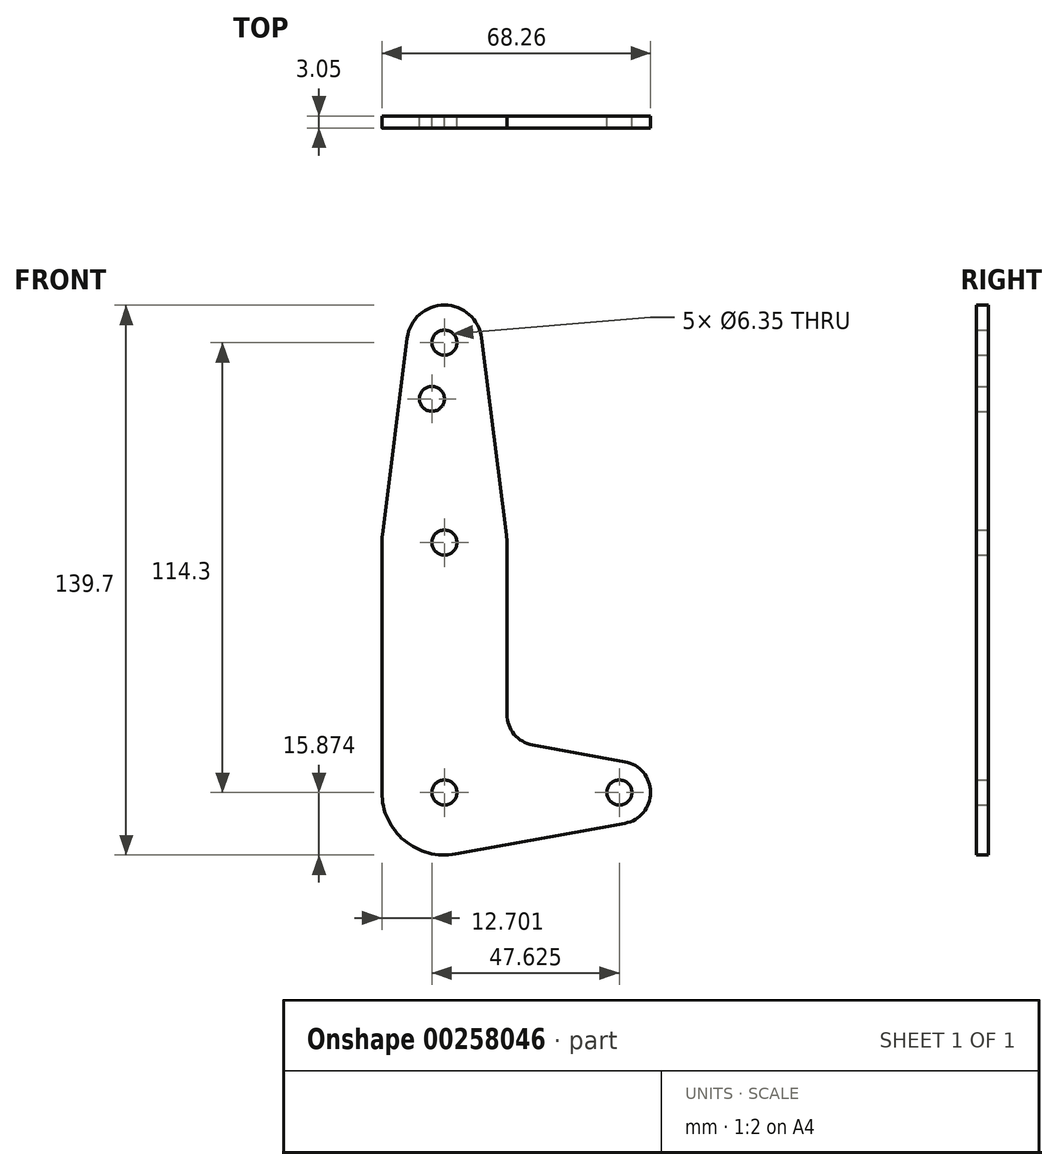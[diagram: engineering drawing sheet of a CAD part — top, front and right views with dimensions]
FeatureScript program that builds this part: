
annotation { "Feature Type Name" : "Feature", "Feature Type Description" : "" }
export const myFeature = defineFeature(function(context is Context, id is Id, definition is map)
    precondition{}
    {
        {
            var Q0;
            Q0=qCreatedBy(makeId("Front.planeOp"),FACE);
            var sketch = newSketch(context, id + "F0", { "sketchPlane" : qUnion([Q0])});
            skLineSegment(sketch, "E0", {"start": v(-37.27, -27.03) * mm, "end": v(-37.27, 87.27) * mm, "construction": true});
            skLineSegment(sketch, "E1", {"start": v(-37.27, -27.03) * mm, "end": v(7.18, -27.03) * mm, "construction": true});
            skCircle(sketch, "E2", {"center": v(-37.27, 87.27) * mm, "radius": 9.53 * mm});
            skCircle(sketch, "E3", {"center": v(-37.27, 36.47) * mm, "radius": 15.88 * mm});
            skCircle(sketch, "E4", {"center": v(-37.27, -27.03) * mm, "radius": 15.88 * mm});
            skCircle(sketch, "E5", {"center": v(7.18, -27.03) * mm, "radius": 7.94 * mm});
            skLineSegment(sketch, "E6", {"start": v(-46.72, 88.46) * mm, "end": v(-53.02, 38.46) * mm});
            skLineSegment(sketch, "E7", {"start": v(-27.82, 88.46) * mm, "end": v(-21.52, 38.46) * mm});
            skLineSegment(sketch, "E8", {"start": v(-53.15, 36.47) * mm, "end": v(-53.15, -27.03) * mm});
            skLineSegment(sketch, "E9", {"start": v(-21.4, 36.47) * mm, "end": v(-21.4, -7.14) * mm});
            skLineSegment(sketch, "E10", {"start": v(-14.87, -14.96) * mm, "end": v(8.6, -19.22) * mm});
            skLineSegment(sketch, "E11", {"start": v(-34.44, -42.65) * mm, "end": v(8.6, -34.84) * mm});
            skCircle(sketch, "E12", {"center": v(-37.27, 87.27) * mm, "radius": 3.18 * mm});
            skCircle(sketch, "E13", {"center": v(-40.45, 73) * mm, "radius": 3.18 * mm});
            skCircle(sketch, "E14", {"center": v(-37.27, -27.03) * mm, "radius": 3.18 * mm});
            skCircle(sketch, "E15", {"center": v(7.18, -27.03) * mm, "radius": 3.18 * mm});
            skArc(sketch, "E16.filletArc", {"start": v(-21.4, -7.14) * mm, "mid": v(-19.55, -12.23) * mm, "end": v(-14.87, -14.96) * mm});
            skCircle(sketch, "E17", {"center": v(-37.27, 36.47) * mm, "radius": 3.17 * mm});
            skSolve(sketch);
        }
        {
            var Q0;
            {var subQ1=sQuery(id+"F0.wireOp",EDGE,"E6");Q0=makeQuery(id+"F0.imprint","IMPRINT",FACE,{"disambiguationData":[TD([[makeQuery(id+"F0.imprint","IMPRINT",EDGE,{"derivedFrom":subQ1}),1.0]])]});}
            var Q1;
            Q1=makeQuery(id+"F0.imprint","IMPRINT",FACE,{"disambiguationData":[TD([[makeQuery(id+"F0.imprint","IMPRINT",EDGE,{"derivedFrom":sQuery(id+"F0.wireOp",EDGE,"E12")}),-1.0]])]});
            var Q2;
            Q2=makeQuery(id+"F0.imprint","IMPRINT",FACE,{"disambiguationData":[TD([[makeQuery(id+"F0.imprint","IMPRINT",EDGE,{"derivedFrom":sQuery(id+"F0.wireOp",EDGE,"E17")}),-1.0]])]});
            var Q3;
            {var subQ0=sQuery(id+"F0.wireOp",EDGE,"E8");Q3=makeQuery(id+"F0.imprint","IMPRINT",FACE,{"disambiguationData":[TD([[makeQuery(id+"F0.imprint","IMPRINT",EDGE,{"derivedFrom":subQ0}),1.0]])]});}
            var Q4;
            Q4=makeQuery(id+"F0.imprint","IMPRINT",FACE,{"disambiguationData":[TD([[makeQuery(id+"F0.imprint","IMPRINT",EDGE,{"derivedFrom":sQuery(id+"F0.wireOp",EDGE,"E14")}),-1.0]])]});
            var Q5;
            Q5=makeQuery(id+"F0.imprint","IMPRINT",FACE,{"disambiguationData":[TD([[makeQuery(id+"F0.imprint","IMPRINT",EDGE,{"derivedFrom":sQuery(id+"F0.wireOp",EDGE,"E15")}),-1.0]])]});
            extrude(context, id + "F1", {"entities" : qUnion([Q0, Q1, Q2, Q3, Q4, Q5]), "depth" : 3.05 * mm});
        }
    });
